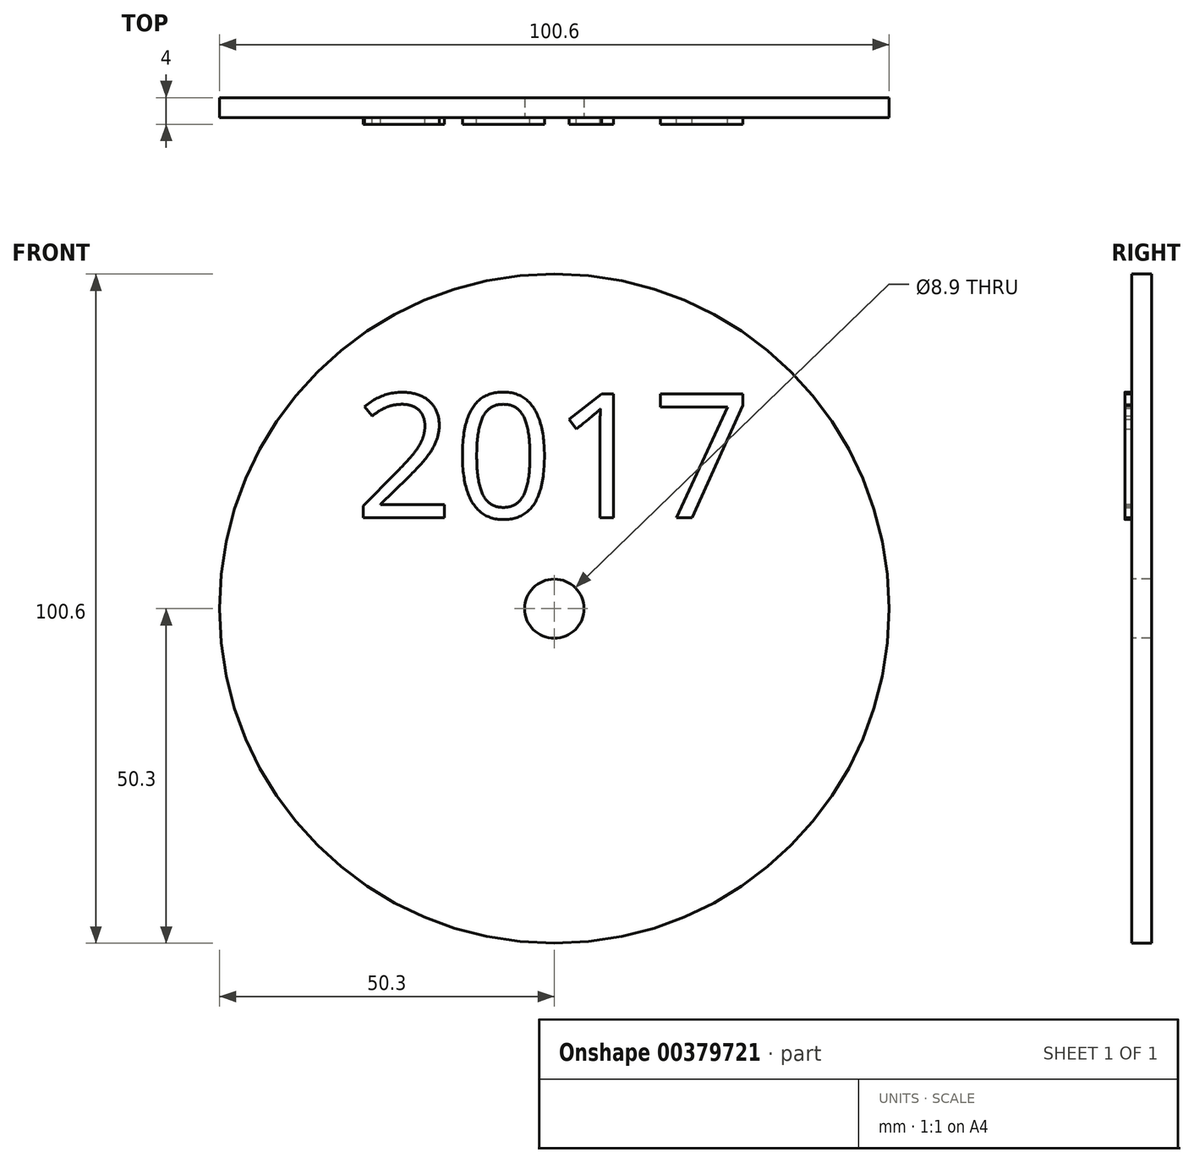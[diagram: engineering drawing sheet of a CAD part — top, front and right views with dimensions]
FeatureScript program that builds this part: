
annotation { "Feature Type Name" : "Feature", "Feature Type Description" : "" }
export const myFeature = defineFeature(function(context is Context, id is Id, definition is map)
    precondition{}
    {
        {
            var Q0;
            Q0=qCreatedBy(makeId("Front.planeOp"),FACE);
            var sketch = newSketch(context, id + "F0", { "sketchPlane" : qUnion([Q0])});
            skCircle(sketch, "E0", {"center": v(0, 0) * mm, "radius": 50.3 * mm});
            skSolve(sketch);
        }
        {
            var Q0;
            Q0 = qSketchRegion(id + "F0", true);
            extrude(context, id + "F1", {"entities" : qUnion([Q0]), "depth" : 3 * mm});
        }
        {
            var Q0;
            Q0=makeQuery(id+"F1.opExtrude","CAP_FACE",FACE,{"disambiguationData":[OSD([sQuery(id+"F0.wireOp",EDGE,"E0")])],"isStart":false});
            var sketch = newSketch(context, id + "F2", { "sketchPlane" : qUnion([Q0])});
            skCircle(sketch, "E1", {"center": v(0, 0) * mm, "radius": 4.45 * mm});
            skSolve(sketch);
        }
        {
            var Q0;
            Q0 = qSketchRegion(id + "F2", true);
            extrude(context, id + "F3", {"entities" : qUnion([Q0]), "operationType" : NewBodyOperationType.REMOVE, "oppositeDirection" : true, "depth" : 25 * mm});
        }
        {
            var Q0;
            Q0=makeQuery(id+"F1.opExtrude","CAP_FACE",FACE,{"disambiguationData":[OSD([sQuery(id+"F0.wireOp",EDGE,"E0")])],"isStart":false});
            var sketch = newSketch(context, id + "F4", { "sketchPlane" : qUnion([Q0])});
            skText(sketch, "E2", { "text": "2017", "fontName": "OpenSans-Regular.ttf"});
            const initialGuessF4  = {"E2": [-0.03, 0.01365, 1, 0, 0.01877]};
            skSetInitialGuess(sketch, initialGuessF4);
            skSolve(sketch);
        }
        {
            var Q0;
            Q0 = qSketchRegion(id + "F4", true);
            extrude(context, id + "F5", {"entities" : qUnion([Q0]), "operationType" : NewBodyOperationType.ADD, "depth" : 1 * mm});
        }
    });
